# Revit family: Haworth_Masters_Cushion
name_source: partatom
category: Furniture Systems
revit_build: Autodesk Revit 2018 (Build: 20170223_1515(x64)
units: mm (PartAtom-declared; Revit-internal decimal feet)

## family parameters
Always vertical = Yes
Cut with Voids When Loaded = No
OmniClass Number = 23.40.70.14
OmniClass Title = Retail and Commercial Equipment and Furnishings
Part Type = Normal
Room Calculation Point = No
Round Connector Dimension = Use Diameter
Shared = No
Work Plane-Based = No

## types (7) — shared parameters
Actual Height = 1 1/4"
Assembly Code = E2020200
Manufacturer = Haworth
Min/Max Depth = 19, 21, 24 in.
Min/Max Width = 15.5, 30, 36, 42 in.
Model = XZSC
OmniClass Number = 23.40.70.14
Revision Number = 2
Size = Verify Final Dim. w/ Haworth
Sustainability Info = https://www.haworth.com
URL = www.haworth.com
URL - Product = https://www.haworth.com
Warranty = https://www.haworth.com

## per-type parameters (varying)
| type | Actual Depth | Actual Width | Description |
| 24d 42w | 24" | 42" | Haworth Masters - Storage Cushion - 24d 42w |
| 24d 36w | 24" | 36" | Haworth Masters - Storage Cushion - 24d 36w |
| 24d 30w | 24" | 30" | Haworth Masters - Storage Cushion - 24d 30w |
| 19d 42w | 19" | 42" | Haworth Masters - Storage Cushion - 19d 42w |
| 19d 36w | 19" | 36" | Haworth Masters - Storage Cushion - 19d 36w |
| 19d 30w | 19" | 30" | Haworth Masters - Storage Cushion - 19d 30w |
| 21d 15w | 21" | 15 1/2" | Haworth Masters - Storage Cushion - 21d 15.4w |

## geometry (parser evidence)
native form markers: Sweep x2
no freeform markers — native parametric forms only
